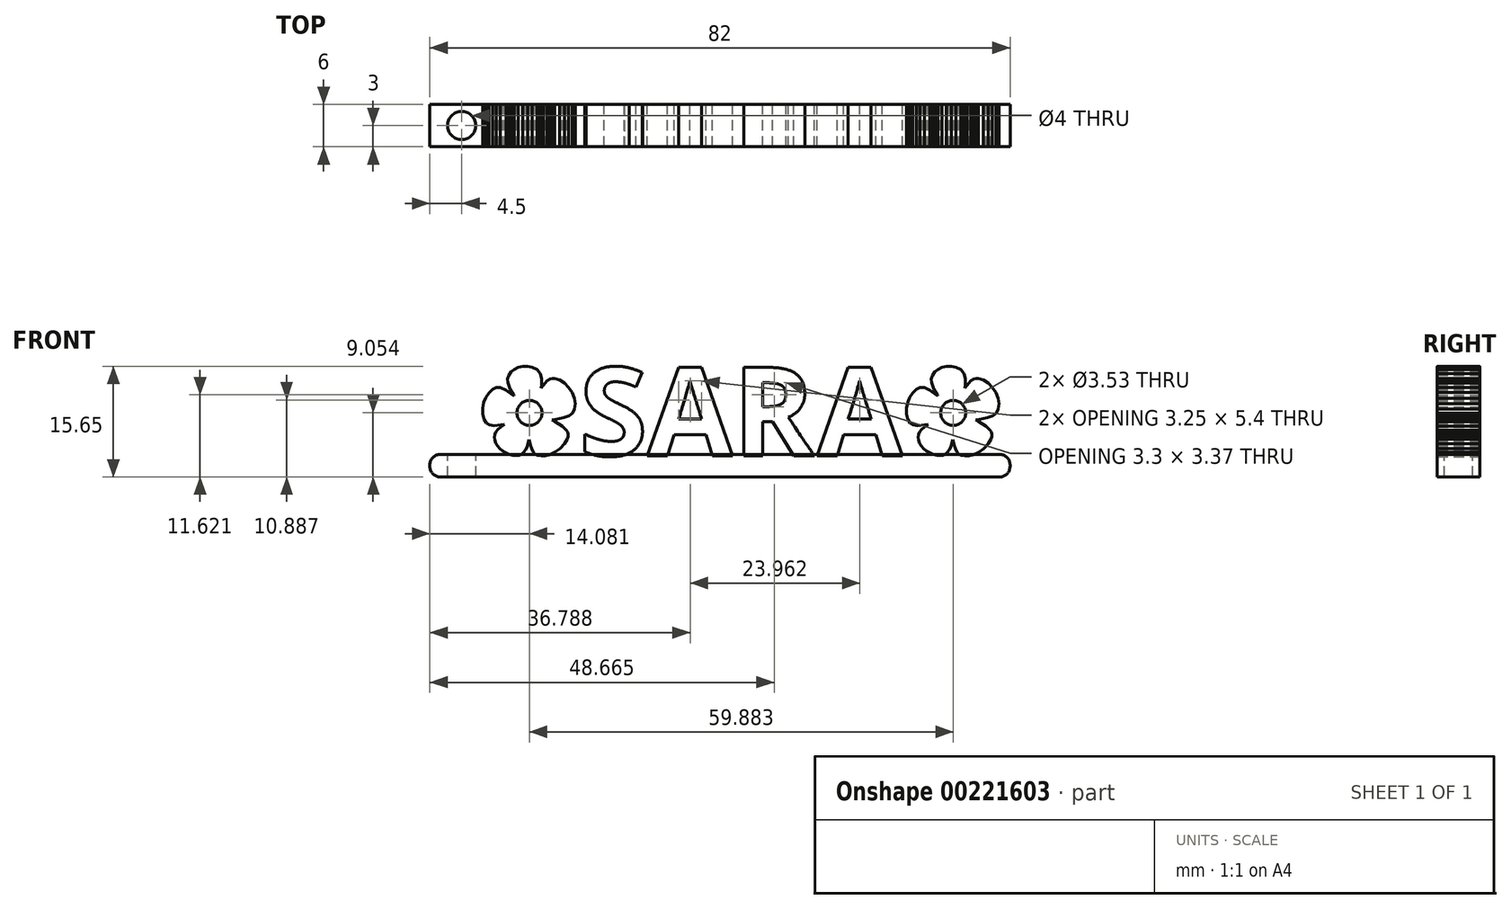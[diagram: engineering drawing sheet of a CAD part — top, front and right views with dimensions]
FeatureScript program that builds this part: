
annotation { "Feature Type Name" : "Feature", "Feature Type Description" : "" }
export const myFeature = defineFeature(function(context is Context, id is Id, definition is map)
    precondition{}
    {
        {
            var Q0;
            Q0=qCreatedBy(makeId("Front.planeOp"),FACE);
            var sketch = newSketch(context, id + "F0", { "sketchPlane" : qUnion([Q0])});
            skText(sketch, "E0", { "text": "   SARA", "fontName": "OpenSans-Bold.ttf"});
            skLineSegment(sketch, "E1.0.0", {"start": v(-9.3, 0.1) * mm, "end": v(-8.53, 0.46) * mm});
            skLineSegment(sketch, "E1.0.1", {"start": v(-8.53, 0.46) * mm, "end": v(-7.79, 1.02) * mm});
            skLineSegment(sketch, "E1.0.2", {"start": v(-7.79, 1.02) * mm, "end": v(-7.18, 1.67) * mm});
            skLineSegment(sketch, "E1.0.3", {"start": v(-7.18, 1.67) * mm, "end": v(-6.78, 2.35) * mm});
            skLineSegment(sketch, "E1.0.4", {"start": v(-6.78, 2.35) * mm, "end": v(-6.68, 2.7) * mm});
            skLineSegment(sketch, "E1.0.5", {"start": v(-6.68, 2.7) * mm, "end": v(-6.67, 3.02) * mm});
            skLineSegment(sketch, "E1.0.6", {"start": v(-6.67, 3.02) * mm, "end": v(-6.73, 3.33) * mm});
            skLineSegment(sketch, "E1.0.7", {"start": v(-6.73, 3.33) * mm, "end": v(-6.89, 3.62) * mm});
            skLineSegment(sketch, "E1.0.8", {"start": v(-6.89, 3.62) * mm, "end": v(-7.48, 4.2) * mm});
            skLineSegment(sketch, "E1.0.9", {"start": v(-7.48, 4.2) * mm, "end": v(-8.5, 4.79) * mm});
            skLineSegment(sketch, "E1.0.10", {"start": v(-8.5, 4.79) * mm, "end": v(-8.93, 5.06) * mm});
            skLineSegment(sketch, "E1.0.11", {"start": v(-8.93, 5.06) * mm, "end": v(-8.42, 5.16) * mm});
            skLineSegment(sketch, "E1.0.12", {"start": v(-8.42, 5.16) * mm, "end": v(-7.31, 5.37) * mm});
            skLineSegment(sketch, "E1.0.13", {"start": v(-7.31, 5.37) * mm, "end": v(-6.55, 5.65) * mm});
            skLineSegment(sketch, "E1.0.14", {"start": v(-6.55, 5.65) * mm, "end": v(-6.05, 6.04) * mm});
            skLineSegment(sketch, "E1.0.15", {"start": v(-6.05, 6.04) * mm, "end": v(-5.76, 6.58) * mm});
            skLineSegment(sketch, "E1.0.16", {"start": v(-5.76, 6.58) * mm, "end": v(-5.64, 7.33) * mm});
            skLineSegment(sketch, "E1.0.17", {"start": v(-5.64, 7.33) * mm, "end": v(-5.78, 8.14) * mm});
            skLineSegment(sketch, "E1.0.18", {"start": v(-5.78, 8.14) * mm, "end": v(-6.1, 8.93) * mm});
            skLineSegment(sketch, "E1.0.19", {"start": v(-6.1, 8.93) * mm, "end": v(-6.6, 9.67) * mm});
            skLineSegment(sketch, "E1.0.20", {"start": v(-6.6, 9.67) * mm, "end": v(-7.2, 10.28) * mm});
            skLineSegment(sketch, "E1.0.21", {"start": v(-7.2, 10.28) * mm, "end": v(-7.86, 10.72) * mm});
            skLineSegment(sketch, "E1.0.22", {"start": v(-7.86, 10.72) * mm, "end": v(-8.55, 10.93) * mm});
            skLineSegment(sketch, "E1.0.23", {"start": v(-8.55, 10.93) * mm, "end": v(-8.88, 10.93) * mm});
            skLineSegment(sketch, "E1.0.24", {"start": v(-8.88, 10.93) * mm, "end": v(-9.2, 10.85) * mm});
            skLineSegment(sketch, "E1.0.25", {"start": v(-9.2, 10.85) * mm, "end": v(-9.65, 10.56) * mm});
            skLineSegment(sketch, "E1.0.26", {"start": v(-9.65, 10.56) * mm, "end": v(-10.14, 9.98) * mm});
            skLineSegment(sketch, "E1.0.27", {"start": v(-10.14, 9.98) * mm, "end": v(-10.45, 9.58) * mm});
            skLineSegment(sketch, "E1.0.28", {"start": v(-10.45, 9.58) * mm, "end": v(-10.4, 10.03) * mm});
            skLineSegment(sketch, "E1.0.29", {"start": v(-10.4, 10.03) * mm, "end": v(-10.4, 10.93) * mm});
            skLineSegment(sketch, "E1.0.30", {"start": v(-10.4, 10.93) * mm, "end": v(-10.6, 11.63) * mm});
            skLineSegment(sketch, "E1.0.31", {"start": v(-10.6, 11.63) * mm, "end": v(-11.04, 12.15) * mm});
            skLineSegment(sketch, "E1.0.32", {"start": v(-11.04, 12.15) * mm, "end": v(-11.71, 12.5) * mm});
            skLineSegment(sketch, "E1.0.33", {"start": v(-11.71, 12.5) * mm, "end": v(-12.4, 12.64) * mm});
            skLineSegment(sketch, "E1.0.34", {"start": v(-12.4, 12.64) * mm, "end": v(-13.07, 12.62) * mm});
            skLineSegment(sketch, "E1.0.35", {"start": v(-13.07, 12.62) * mm, "end": v(-13.7, 12.47) * mm});
            skLineSegment(sketch, "E1.0.36", {"start": v(-13.7, 12.47) * mm, "end": v(-14.26, 12.2) * mm});
            skLineSegment(sketch, "E1.0.37", {"start": v(-14.26, 12.2) * mm, "end": v(-14.72, 11.83) * mm});
            skLineSegment(sketch, "E1.0.38", {"start": v(-14.72, 11.83) * mm, "end": v(-15.05, 11.38) * mm});
            skLineSegment(sketch, "E1.0.39", {"start": v(-15.05, 11.38) * mm, "end": v(-15.22, 10.87) * mm});
            skLineSegment(sketch, "E1.0.40", {"start": v(-15.22, 10.87) * mm, "end": v(-15.2, 10.3) * mm});
            skLineSegment(sketch, "E1.0.41", {"start": v(-15.2, 10.3) * mm, "end": v(-14.83, 9.4) * mm});
            skLineSegment(sketch, "E1.0.42", {"start": v(-14.83, 9.4) * mm, "end": v(-14.35, 8.55) * mm});
            skLineSegment(sketch, "E1.0.43", {"start": v(-14.35, 8.55) * mm, "end": v(-14.3, 8.4) * mm});
            skLineSegment(sketch, "E1.0.44", {"start": v(-14.3, 8.4) * mm, "end": v(-14.48, 8.53) * mm});
            skLineSegment(sketch, "E1.0.45", {"start": v(-14.48, 8.53) * mm, "end": v(-15.4, 9.23) * mm});
            skLineSegment(sketch, "E1.0.46", {"start": v(-15.4, 9.23) * mm, "end": v(-16.22, 9.63) * mm});
            skLineSegment(sketch, "E1.0.47", {"start": v(-16.22, 9.63) * mm, "end": v(-16.8, 9.63) * mm});
            skLineSegment(sketch, "E1.0.48", {"start": v(-16.8, 9.63) * mm, "end": v(-17.36, 9.37) * mm});
            skLineSegment(sketch, "E1.0.49", {"start": v(-17.36, 9.37) * mm, "end": v(-17.85, 8.9) * mm});
            skLineSegment(sketch, "E1.0.50", {"start": v(-17.85, 8.9) * mm, "end": v(-18.26, 8.26) * mm});
            skLineSegment(sketch, "E1.0.51", {"start": v(-18.26, 8.26) * mm, "end": v(-18.56, 7.51) * mm});
            skLineSegment(sketch, "E1.0.52", {"start": v(-18.56, 7.51) * mm, "end": v(-18.72, 6.71) * mm});
            skLineSegment(sketch, "E1.0.53", {"start": v(-18.72, 6.71) * mm, "end": v(-18.72, 5.9) * mm});
            skLineSegment(sketch, "E1.0.54", {"start": v(-18.72, 5.9) * mm, "end": v(-18.52, 5.16) * mm});
            skLineSegment(sketch, "E1.0.55", {"start": v(-18.52, 5.16) * mm, "end": v(-18.2, 4.64) * mm});
            skLineSegment(sketch, "E1.0.56", {"start": v(-18.2, 4.64) * mm, "end": v(-17.75, 4.36) * mm});
            skLineSegment(sketch, "E1.0.57", {"start": v(-17.75, 4.36) * mm, "end": v(-17.1, 4.27) * mm});
            skLineSegment(sketch, "E1.0.58", {"start": v(-17.1, 4.27) * mm, "end": v(-16.21, 4.37) * mm});
            skLineSegment(sketch, "E1.0.59", {"start": v(-16.21, 4.37) * mm, "end": v(-15.7, 4.43) * mm});
            skLineSegment(sketch, "E1.0.60", {"start": v(-15.7, 4.43) * mm, "end": v(-15.67, 4.4) * mm});
            skLineSegment(sketch, "E1.0.61", {"start": v(-15.67, 4.4) * mm, "end": v(-15.78, 4.33) * mm});
            skLineSegment(sketch, "E1.0.62", {"start": v(-15.78, 4.33) * mm, "end": v(-16.17, 4.07) * mm});
            skLineSegment(sketch, "E1.0.63", {"start": v(-16.17, 4.07) * mm, "end": v(-16.55, 3.71) * mm});
            skLineSegment(sketch, "E1.0.64", {"start": v(-16.55, 3.71) * mm, "end": v(-16.87, 3.33) * mm});
            skLineSegment(sketch, "E1.0.65", {"start": v(-16.87, 3.33) * mm, "end": v(-17.04, 3) * mm});
            skLineSegment(sketch, "E1.0.66", {"start": v(-17.04, 3) * mm, "end": v(-17.08, 2.6) * mm});
            skLineSegment(sketch, "E1.0.67", {"start": v(-17.08, 2.6) * mm, "end": v(-17.02, 2.2) * mm});
            skLineSegment(sketch, "E1.0.68", {"start": v(-17.02, 2.2) * mm, "end": v(-16.87, 1.78) * mm});
            skLineSegment(sketch, "E1.0.69", {"start": v(-16.87, 1.78) * mm, "end": v(-16.62, 1.39) * mm});
            skLineSegment(sketch, "E1.0.70", {"start": v(-16.62, 1.39) * mm, "end": v(-16.3, 1.02) * mm});
            skLineSegment(sketch, "E1.0.71", {"start": v(-16.3, 1.02) * mm, "end": v(-15.9, 0.69) * mm});
            skLineSegment(sketch, "E1.0.72", {"start": v(-15.9, 0.69) * mm, "end": v(-15.45, 0.4) * mm});
            skLineSegment(sketch, "E1.0.73", {"start": v(-15.45, 0.4) * mm, "end": v(-14.95, 0.2) * mm});
            skLineSegment(sketch, "E1.0.74", {"start": v(-14.95, 0.2) * mm, "end": v(-14.44, 0.06) * mm});
            skLineSegment(sketch, "E1.0.75", {"start": v(-14.44, 0.06) * mm, "end": v(-13.98, 0.02) * mm});
            skLineSegment(sketch, "E1.0.76", {"start": v(-13.98, 0.02) * mm, "end": v(-13.58, 0.08) * mm});
            skLineSegment(sketch, "E1.0.77", {"start": v(-13.58, 0.08) * mm, "end": v(-13.23, 0.23) * mm});
            skLineSegment(sketch, "E1.0.78", {"start": v(-13.23, 0.23) * mm, "end": v(-12.92, 0.49) * mm});
            skLineSegment(sketch, "E1.0.79", {"start": v(-12.92, 0.49) * mm, "end": v(-12.67, 0.84) * mm});
            skLineSegment(sketch, "E1.0.80", {"start": v(-12.67, 0.84) * mm, "end": v(-12.46, 1.28) * mm});
            skLineSegment(sketch, "E1.0.81", {"start": v(-12.46, 1.28) * mm, "end": v(-12.3, 1.83) * mm});
            skLineSegment(sketch, "E1.0.82", {"start": v(-12.3, 1.83) * mm, "end": v(-12.19, 2.26) * mm});
            skLineSegment(sketch, "E1.0.83", {"start": v(-12.19, 2.26) * mm, "end": v(-12.13, 2.1) * mm});
            skLineSegment(sketch, "E1.0.84", {"start": v(-12.13, 2.1) * mm, "end": v(-12.01, 1.53) * mm});
            skLineSegment(sketch, "E1.0.85", {"start": v(-12.01, 1.53) * mm, "end": v(-11.82, 1) * mm});
            skLineSegment(sketch, "E1.0.86", {"start": v(-11.82, 1) * mm, "end": v(-11.6, 0.55) * mm});
            skLineSegment(sketch, "E1.0.87", {"start": v(-11.6, 0.55) * mm, "end": v(-11.35, 0.26) * mm});
            skLineSegment(sketch, "E1.0.88", {"start": v(-11.35, 0.26) * mm, "end": v(-10.95, 0.05) * mm});
            skLineSegment(sketch, "E1.0.89", {"start": v(-10.95, 0.05) * mm, "end": v(-10.46, -0.04) * mm});
            skLineSegment(sketch, "E1.0.90", {"start": v(-10.46, -0.04) * mm, "end": v(-9.9, -0.03) * mm});
            skLineSegment(sketch, "E1.0.91", {"start": v(-9.9, -0.03) * mm, "end": v(-9.3, 0.1) * mm});
            skCircle(sketch, "E2", {"center": v(-12.12, 6.05) * mm, "radius": 1.77 * mm});
            skCircle(sketch, "E3.1.0.0", {"center": v(47.76, 6.05) * mm, "radius": 1.77 * mm});
            skLineSegment(sketch, "E3.1.0.1", {"start": v(49.43, 9.58) * mm, "end": v(49.48, 10.03) * mm});
            skLineSegment(sketch, "E3.1.0.2", {"start": v(52.69, 10.28) * mm, "end": v(52.02, 10.72) * mm});
            skLineSegment(sketch, "E3.1.0.3", {"start": v(41.17, 5.9) * mm, "end": v(41.37, 5.16) * mm});
            skLineSegment(sketch, "E3.1.0.4", {"start": v(45.62, 12.2) * mm, "end": v(45.16, 11.83) * mm});
            skLineSegment(sketch, "E3.1.0.5", {"start": v(43.58, 1.02) * mm, "end": v(43.98, 0.69) * mm});
            skLineSegment(sketch, "E3.1.0.6", {"start": v(43.67, 9.63) * mm, "end": v(43.08, 9.63) * mm});
            skLineSegment(sketch, "E3.1.0.7", {"start": v(41.32, 7.51) * mm, "end": v(41.16, 6.71) * mm});
            skLineSegment(sketch, "E3.1.0.8", {"start": v(44.49, 9.23) * mm, "end": v(43.67, 9.63) * mm});
            skLineSegment(sketch, "E3.1.0.9", {"start": v(43.08, 9.63) * mm, "end": v(42.53, 9.37) * mm});
            skLineSegment(sketch, "E3.1.0.10", {"start": v(49.74, 9.98) * mm, "end": v(49.43, 9.58) * mm});
            skLineSegment(sketch, "E3.1.0.11", {"start": v(49.28, 11.63) * mm, "end": v(48.85, 12.15) * mm});
            skLineSegment(sketch, "E3.1.0.12", {"start": v(48.85, 12.15) * mm, "end": v(48.17, 12.5) * mm});
            skLineSegment(sketch, "E3.1.0.13", {"start": v(49.5, 10.93) * mm, "end": v(49.28, 11.63) * mm});
            skLineSegment(sketch, "E3.1.0.14", {"start": v(44.43, 0.4) * mm, "end": v(44.94, 0.2) * mm});
            skLineSegment(sketch, "E3.1.0.15", {"start": v(49.99, -0.03) * mm, "end": v(50.57, 0.1) * mm});
            skLineSegment(sketch, "E3.1.0.16", {"start": v(41.16, 6.71) * mm, "end": v(41.17, 5.9) * mm});
            skLineSegment(sketch, "E3.1.0.17", {"start": v(50.57, 0.1) * mm, "end": v(51.35, 0.46) * mm});
            skLineSegment(sketch, "E3.1.0.18", {"start": v(43.98, 0.69) * mm, "end": v(44.43, 0.4) * mm});
            skLineSegment(sketch, "E3.1.0.19", {"start": v(41.37, 5.16) * mm, "end": v(41.68, 4.64) * mm});
            skLineSegment(sketch, "E3.1.0.20", {"start": v(52.57, 5.37) * mm, "end": v(53.34, 5.65) * mm});
            skLineSegment(sketch, "E3.1.0.21", {"start": v(51.35, 0.46) * mm, "end": v(52.1, 1.02) * mm});
            skLineSegment(sketch, "E3.1.0.22", {"start": v(53.29, 9.67) * mm, "end": v(52.69, 10.28) * mm});
            skLineSegment(sketch, "E3.1.0.23", {"start": v(49.48, 10.03) * mm, "end": v(49.5, 10.93) * mm});
            skLineSegment(sketch, "E3.1.0.24", {"start": v(42.53, 9.37) * mm, "end": v(42.03, 8.9) * mm});
            skLineSegment(sketch, "E3.1.0.25", {"start": v(48.17, 12.5) * mm, "end": v(47.49, 12.64) * mm});
            skLineSegment(sketch, "E3.1.0.26", {"start": v(46.81, 12.62) * mm, "end": v(46.18, 12.47) * mm});
            skLineSegment(sketch, "E3.1.0.27", {"start": v(52.7, 1.67) * mm, "end": v(53.1, 2.35) * mm});
            skLineSegment(sketch, "E3.1.0.28", {"start": v(53.77, 8.93) * mm, "end": v(53.29, 9.67) * mm});
            skLineSegment(sketch, "E3.1.0.29", {"start": v(47.49, 12.64) * mm, "end": v(46.81, 12.62) * mm});
            skLineSegment(sketch, "E3.1.0.30", {"start": v(52.1, 1.02) * mm, "end": v(52.7, 1.67) * mm});
            skLineSegment(sketch, "E3.1.0.31", {"start": v(42.03, 8.9) * mm, "end": v(41.62, 8.26) * mm});
            skLineSegment(sketch, "E3.1.0.32", {"start": v(41.62, 8.26) * mm, "end": v(41.32, 7.51) * mm});
            skLineSegment(sketch, "E3.1.0.33", {"start": v(46.18, 12.47) * mm, "end": v(45.62, 12.2) * mm});
            skLineSegment(sketch, "E3.1.0.34", {"start": v(53.1, 2.35) * mm, "end": v(53.2, 2.7) * mm});
            skLineSegment(sketch, "E3.1.0.35", {"start": v(43.08, 9.63) * mm, "end": v(42.53, 9.37) * mm});
            skLineSegment(sketch, "E3.1.0.36", {"start": v(47.49, 12.64) * mm, "end": v(46.81, 12.62) * mm});
            skLineSegment(sketch, "E3.1.0.37", {"start": v(52.57, 5.37) * mm, "end": v(53.34, 5.65) * mm});
            skLineSegment(sketch, "E3.1.0.38", {"start": v(48.93, 0.05) * mm, "end": v(49.43, -0.04) * mm});
            skLineSegment(sketch, "E3.1.0.39", {"start": v(53.77, 8.93) * mm, "end": v(53.29, 9.67) * mm});
            skLineSegment(sketch, "E3.1.0.40", {"start": v(49.99, -0.03) * mm, "end": v(50.57, 0.1) * mm});
            skLineSegment(sketch, "E3.1.0.41", {"start": v(49.74, 9.98) * mm, "end": v(49.43, 9.58) * mm});
            skLineSegment(sketch, "E3.1.0.42", {"start": v(52.1, 1.02) * mm, "end": v(52.7, 1.67) * mm});
            skLineSegment(sketch, "E3.1.0.43", {"start": v(53.1, 2.35) * mm, "end": v(53.2, 2.7) * mm});
            skLineSegment(sketch, "E3.1.0.44", {"start": v(41.16, 6.71) * mm, "end": v(41.17, 5.9) * mm});
            skLineSegment(sketch, "E3.1.0.45", {"start": v(50.57, 0.1) * mm, "end": v(51.35, 0.46) * mm});
            skLineSegment(sketch, "E3.1.0.46", {"start": v(46.81, 12.62) * mm, "end": v(46.18, 12.47) * mm});
            skLineSegment(sketch, "E3.1.0.47", {"start": v(45.62, 12.2) * mm, "end": v(45.16, 11.83) * mm});
            skLineSegment(sketch, "E3.1.0.48", {"start": v(44.43, 0.4) * mm, "end": v(44.94, 0.2) * mm});
            skLineSegment(sketch, "E3.1.0.49", {"start": v(49.48, 10.03) * mm, "end": v(49.5, 10.93) * mm});
            skLineSegment(sketch, "E3.1.0.50", {"start": v(49.43, 9.58) * mm, "end": v(49.48, 10.03) * mm});
            skLineSegment(sketch, "E3.1.0.51", {"start": v(49.43, -0.04) * mm, "end": v(49.99, -0.03) * mm});
            skLineSegment(sketch, "E3.1.0.52", {"start": v(43.67, 9.63) * mm, "end": v(43.08, 9.63) * mm});
            skLineSegment(sketch, "E3.1.0.53", {"start": v(49.5, 10.93) * mm, "end": v(49.28, 11.63) * mm});
            skLineSegment(sketch, "E3.1.0.54", {"start": v(52.69, 10.28) * mm, "end": v(52.02, 10.72) * mm});
            skLineSegment(sketch, "E3.1.0.55", {"start": v(42.03, 8.9) * mm, "end": v(41.62, 8.26) * mm});
            skLineSegment(sketch, "E3.1.0.56", {"start": v(43.98, 0.69) * mm, "end": v(44.43, 0.4) * mm});
            skLineSegment(sketch, "E3.1.0.57", {"start": v(48.17, 12.5) * mm, "end": v(47.49, 12.64) * mm});
            skLineSegment(sketch, "E3.1.0.58", {"start": v(42.53, 9.37) * mm, "end": v(42.03, 8.9) * mm});
            skLineSegment(sketch, "E3.1.0.59", {"start": v(41.17, 5.9) * mm, "end": v(41.37, 5.16) * mm});
            skLineSegment(sketch, "E3.1.0.60", {"start": v(48.85, 12.15) * mm, "end": v(48.17, 12.5) * mm});
            skLineSegment(sketch, "E3.1.0.61", {"start": v(44.49, 9.23) * mm, "end": v(43.67, 9.63) * mm});
            skLineSegment(sketch, "E3.1.0.62", {"start": v(51.35, 0.46) * mm, "end": v(52.1, 1.02) * mm});
            skLineSegment(sketch, "E3.1.0.63", {"start": v(49.28, 11.63) * mm, "end": v(48.85, 12.15) * mm});
            skLineSegment(sketch, "E3.1.0.64", {"start": v(41.62, 8.26) * mm, "end": v(41.32, 7.51) * mm});
            skLineSegment(sketch, "E3.1.0.65", {"start": v(52.7, 1.67) * mm, "end": v(53.1, 2.35) * mm});
            skLineSegment(sketch, "E3.1.0.66", {"start": v(41.32, 7.51) * mm, "end": v(41.16, 6.71) * mm});
            skLineSegment(sketch, "E3.1.0.67", {"start": v(43.58, 1.02) * mm, "end": v(43.98, 0.69) * mm});
            skLineSegment(sketch, "E3.1.0.68", {"start": v(41.37, 5.16) * mm, "end": v(41.68, 4.64) * mm});
            skLineSegment(sketch, "E3.1.0.69", {"start": v(46.18, 12.47) * mm, "end": v(45.62, 12.2) * mm});
            skLineSegment(sketch, "E3.1.0.70", {"start": v(53.29, 9.67) * mm, "end": v(52.69, 10.28) * mm});
            skLineSegment(sketch, "E3.1.0.71", {"start": v(45.16, 11.83) * mm, "end": v(44.83, 11.38) * mm});
            skLineSegment(sketch, "E3.1.0.72", {"start": v(52.02, 10.72) * mm, "end": v(51.34, 10.93) * mm});
            skLineSegment(sketch, "E3.1.0.73", {"start": v(53.83, 6.04) * mm, "end": v(54.13, 6.58) * mm});
            skLineSegment(sketch, "E3.1.0.74", {"start": v(53.2, 2.7) * mm, "end": v(53.22, 3.02) * mm});
            skLineSegment(sketch, "E3.1.0.75", {"start": v(51.34, 10.93) * mm, "end": v(51, 10.93) * mm});
            skLineSegment(sketch, "E3.1.0.76", {"start": v(41.68, 4.64) * mm, "end": v(42.13, 4.36) * mm});
            skLineSegment(sketch, "E3.1.0.77", {"start": v(50.68, 10.85) * mm, "end": v(50.24, 10.56) * mm});
            skLineSegment(sketch, "E3.1.0.78", {"start": v(51.47, 5.16) * mm, "end": v(52.57, 5.37) * mm});
            skLineSegment(sketch, "E3.1.0.79", {"start": v(53.22, 3.02) * mm, "end": v(53.15, 3.33) * mm});
            skLineSegment(sketch, "E3.1.0.80", {"start": v(53.15, 3.33) * mm, "end": v(53, 3.62) * mm});
            skLineSegment(sketch, "E3.1.0.81", {"start": v(52.4, 4.2) * mm, "end": v(51.39, 4.79) * mm});
            skLineSegment(sketch, "E3.1.0.82", {"start": v(54.24, 7.33) * mm, "end": v(54.1, 8.14) * mm});
            skLineSegment(sketch, "E3.1.0.83", {"start": v(43.26, 1.39) * mm, "end": v(43.58, 1.02) * mm});
            skLineSegment(sketch, "E3.1.0.84", {"start": v(45.44, 0.06) * mm, "end": v(45.9, 0.02) * mm});
            skLineSegment(sketch, "E3.1.0.85", {"start": v(50.96, 5.06) * mm, "end": v(51.47, 5.16) * mm});
            skLineSegment(sketch, "E3.1.0.86", {"start": v(48.53, 0.26) * mm, "end": v(48.93, 0.05) * mm});
            skLineSegment(sketch, "E3.1.0.87", {"start": v(44.83, 11.38) * mm, "end": v(44.66, 10.87) * mm});
            skLineSegment(sketch, "E3.1.0.88", {"start": v(54.13, 6.58) * mm, "end": v(54.24, 7.33) * mm});
            skLineSegment(sketch, "E3.1.0.89", {"start": v(48.93, 0.05) * mm, "end": v(49.43, -0.04) * mm});
            skLineSegment(sketch, "E3.1.0.90", {"start": v(51.39, 4.79) * mm, "end": v(50.96, 5.06) * mm});
            skLineSegment(sketch, "E3.1.0.91", {"start": v(44.94, 0.2) * mm, "end": v(45.44, 0.06) * mm});
            skLineSegment(sketch, "E3.1.0.92", {"start": v(44.69, 10.3) * mm, "end": v(45.05, 9.4) * mm});
            skLineSegment(sketch, "E3.1.0.93", {"start": v(43.02, 1.78) * mm, "end": v(43.26, 1.39) * mm});
            skLineSegment(sketch, "E3.1.0.94", {"start": v(53, 3.62) * mm, "end": v(52.4, 4.2) * mm});
            skLineSegment(sketch, "E3.1.0.95", {"start": v(49.43, -0.04) * mm, "end": v(49.99, -0.03) * mm});
            skLineSegment(sketch, "E3.1.0.96", {"start": v(44.66, 10.87) * mm, "end": v(44.69, 10.3) * mm});
            skLineSegment(sketch, "E3.1.0.97", {"start": v(53.34, 5.65) * mm, "end": v(53.83, 6.04) * mm});
            skLineSegment(sketch, "E3.1.0.98", {"start": v(51, 10.93) * mm, "end": v(50.68, 10.85) * mm});
            skLineSegment(sketch, "E3.1.0.99", {"start": v(50.24, 10.56) * mm, "end": v(49.74, 9.98) * mm});
            skLineSegment(sketch, "E3.1.0.100", {"start": v(45.9, 0.02) * mm, "end": v(46.3, 0.08) * mm});
            skLineSegment(sketch, "E3.1.0.101", {"start": v(42.86, 2.2) * mm, "end": v(43.02, 1.78) * mm});
            skLineSegment(sketch, "E3.1.0.102", {"start": v(54.1, 8.14) * mm, "end": v(53.77, 8.93) * mm});
            skLineSegment(sketch, "E3.1.0.103", {"start": v(51.39, 4.79) * mm, "end": v(50.96, 5.06) * mm});
            skLineSegment(sketch, "E3.1.0.104", {"start": v(50.96, 5.06) * mm, "end": v(51.47, 5.16) * mm});
            skLineSegment(sketch, "E3.1.0.105", {"start": v(41.68, 4.64) * mm, "end": v(42.13, 4.36) * mm});
            skLineSegment(sketch, "E3.1.0.106", {"start": v(48.29, 0.55) * mm, "end": v(48.53, 0.26) * mm});
            skLineSegment(sketch, "E3.1.0.107", {"start": v(48.53, 0.26) * mm, "end": v(48.93, 0.05) * mm});
            skLineSegment(sketch, "E3.1.0.108", {"start": v(43.02, 1.78) * mm, "end": v(43.26, 1.39) * mm});
            skLineSegment(sketch, "E3.1.0.109", {"start": v(53, 3.62) * mm, "end": v(52.4, 4.2) * mm});
            skLineSegment(sketch, "E3.1.0.110", {"start": v(51.47, 5.16) * mm, "end": v(52.57, 5.37) * mm});
            skLineSegment(sketch, "E3.1.0.111", {"start": v(44.69, 10.3) * mm, "end": v(45.05, 9.4) * mm});
            skLineSegment(sketch, "E3.1.0.112", {"start": v(53.34, 5.65) * mm, "end": v(53.83, 6.04) * mm});
            skLineSegment(sketch, "E3.1.0.113", {"start": v(50.24, 10.56) * mm, "end": v(49.74, 9.98) * mm});
            skLineSegment(sketch, "E3.1.0.114", {"start": v(54.13, 6.58) * mm, "end": v(54.24, 7.33) * mm});
            skLineSegment(sketch, "E3.1.0.115", {"start": v(44.66, 10.87) * mm, "end": v(44.69, 10.3) * mm});
            skLineSegment(sketch, "E3.1.0.116", {"start": v(51, 10.93) * mm, "end": v(50.68, 10.85) * mm});
            skLineSegment(sketch, "E3.1.0.117", {"start": v(45.9, 0.02) * mm, "end": v(46.3, 0.08) * mm});
            skLineSegment(sketch, "E3.1.0.118", {"start": v(50.68, 10.85) * mm, "end": v(50.24, 10.56) * mm});
            skLineSegment(sketch, "E3.1.0.119", {"start": v(45.44, 0.06) * mm, "end": v(45.9, 0.02) * mm});
            skLineSegment(sketch, "E3.1.0.120", {"start": v(44.94, 0.2) * mm, "end": v(45.44, 0.06) * mm});
            skLineSegment(sketch, "E3.1.0.121", {"start": v(52.4, 4.2) * mm, "end": v(51.39, 4.79) * mm});
            skLineSegment(sketch, "E3.1.0.122", {"start": v(53.83, 6.04) * mm, "end": v(54.13, 6.58) * mm});
            skLineSegment(sketch, "E3.1.0.123", {"start": v(42.8, 2.6) * mm, "end": v(42.86, 2.2) * mm});
            skLineSegment(sketch, "E3.1.0.124", {"start": v(53.2, 2.7) * mm, "end": v(53.22, 3.02) * mm});
            skLineSegment(sketch, "E3.1.0.125", {"start": v(43.26, 1.39) * mm, "end": v(43.58, 1.02) * mm});
            skLineSegment(sketch, "E3.1.0.126", {"start": v(54.1, 8.14) * mm, "end": v(53.77, 8.93) * mm});
            skLineSegment(sketch, "E3.1.0.127", {"start": v(54.24, 7.33) * mm, "end": v(54.1, 8.14) * mm});
            skLineSegment(sketch, "E3.1.0.128", {"start": v(53.22, 3.02) * mm, "end": v(53.15, 3.33) * mm});
            skLineSegment(sketch, "E3.1.0.129", {"start": v(42.86, 2.2) * mm, "end": v(43.02, 1.78) * mm});
            skLineSegment(sketch, "E3.1.0.130", {"start": v(53.15, 3.33) * mm, "end": v(53, 3.62) * mm});
            skLineSegment(sketch, "E3.1.0.131", {"start": v(44.83, 11.38) * mm, "end": v(44.66, 10.87) * mm});
            skLineSegment(sketch, "E3.1.0.132", {"start": v(51.34, 10.93) * mm, "end": v(51, 10.93) * mm});
            skLineSegment(sketch, "E3.1.0.133", {"start": v(52.02, 10.72) * mm, "end": v(51.34, 10.93) * mm});
            skLineSegment(sketch, "E3.1.0.134", {"start": v(45.16, 11.83) * mm, "end": v(44.83, 11.38) * mm});
            skLineSegment(sketch, "E3.1.0.135", {"start": v(42.8, 2.6) * mm, "end": v(42.86, 2.2) * mm});
            skLineSegment(sketch, "E3.1.0.136", {"start": v(43.67, 4.37) * mm, "end": v(44.18, 4.43) * mm});
            skLineSegment(sketch, "E3.1.0.137", {"start": v(47.87, 1.53) * mm, "end": v(48.06, 1) * mm});
            skLineSegment(sketch, "E3.1.0.138", {"start": v(44.1, 4.33) * mm, "end": v(43.72, 4.07) * mm});
            skLineSegment(sketch, "E3.1.0.139", {"start": v(46.66, 0.23) * mm, "end": v(46.96, 0.49) * mm});
            skLineSegment(sketch, "E3.1.0.140", {"start": v(47.22, 0.84) * mm, "end": v(47.42, 1.28) * mm});
            skLineSegment(sketch, "E3.1.0.141", {"start": v(48.06, 1) * mm, "end": v(48.29, 0.55) * mm});
            skLineSegment(sketch, "E3.1.0.142", {"start": v(43.72, 4.07) * mm, "end": v(43.33, 3.71) * mm});
            skLineSegment(sketch, "E3.1.0.143", {"start": v(47.75, 2.1) * mm, "end": v(47.87, 1.53) * mm});
            skLineSegment(sketch, "E3.1.0.144", {"start": v(46.96, 0.49) * mm, "end": v(47.22, 0.84) * mm});
            skLineSegment(sketch, "E3.1.0.145", {"start": v(42.77, 4.27) * mm, "end": v(43.67, 4.37) * mm});
            skLineSegment(sketch, "E3.1.0.146", {"start": v(43.33, 3.71) * mm, "end": v(43.02, 3.33) * mm});
            skLineSegment(sketch, "E3.1.0.147", {"start": v(42.13, 4.36) * mm, "end": v(42.77, 4.27) * mm});
            skLineSegment(sketch, "E3.1.0.148", {"start": v(47.42, 1.28) * mm, "end": v(47.58, 1.83) * mm});
            skLineSegment(sketch, "E3.1.0.149", {"start": v(47.7, 2.26) * mm, "end": v(47.75, 2.1) * mm});
            skLineSegment(sketch, "E3.1.0.150", {"start": v(43.02, 3.33) * mm, "end": v(42.85, 3) * mm});
            skLineSegment(sketch, "E3.1.0.151", {"start": v(48.29, 0.55) * mm, "end": v(48.53, 0.26) * mm});
            skLineSegment(sketch, "E3.1.0.152", {"start": v(47.58, 1.83) * mm, "end": v(47.7, 2.26) * mm});
            skLineSegment(sketch, "E3.1.0.153", {"start": v(42.85, 3) * mm, "end": v(42.8, 2.6) * mm});
            skLineSegment(sketch, "E3.1.0.154", {"start": v(46.3, 0.08) * mm, "end": v(46.66, 0.23) * mm});
            skLineSegment(sketch, "E3.1.0.155", {"start": v(44.21, 4.4) * mm, "end": v(44.1, 4.33) * mm});
            skLineSegment(sketch, "E3.1.0.156", {"start": v(47.7, 2.26) * mm, "end": v(47.75, 2.1) * mm});
            skLineSegment(sketch, "E3.1.0.157", {"start": v(42.77, 4.27) * mm, "end": v(43.67, 4.37) * mm});
            skLineSegment(sketch, "E3.1.0.158", {"start": v(47.87, 1.53) * mm, "end": v(48.06, 1) * mm});
            skLineSegment(sketch, "E3.1.0.159", {"start": v(44.18, 4.43) * mm, "end": v(44.21, 4.4) * mm});
            skLineSegment(sketch, "E3.1.0.160", {"start": v(43.33, 3.71) * mm, "end": v(43.02, 3.33) * mm});
            skLineSegment(sketch, "E3.1.0.161", {"start": v(42.13, 4.36) * mm, "end": v(42.77, 4.27) * mm});
            skLineSegment(sketch, "E3.1.0.162", {"start": v(43.67, 4.37) * mm, "end": v(44.18, 4.43) * mm});
            skLineSegment(sketch, "E3.1.0.163", {"start": v(46.3, 0.08) * mm, "end": v(46.66, 0.23) * mm});
            skLineSegment(sketch, "E3.1.0.164", {"start": v(43.72, 4.07) * mm, "end": v(43.33, 3.71) * mm});
            skLineSegment(sketch, "E3.1.0.165", {"start": v(47.75, 2.1) * mm, "end": v(47.87, 1.53) * mm});
            skLineSegment(sketch, "E3.1.0.166", {"start": v(47.58, 1.83) * mm, "end": v(47.7, 2.26) * mm});
            skLineSegment(sketch, "E3.1.0.167", {"start": v(44.1, 4.33) * mm, "end": v(43.72, 4.07) * mm});
            skLineSegment(sketch, "E3.1.0.168", {"start": v(46.66, 0.23) * mm, "end": v(46.96, 0.49) * mm});
            skLineSegment(sketch, "E3.1.0.169", {"start": v(42.85, 3) * mm, "end": v(42.8, 2.6) * mm});
            skLineSegment(sketch, "E3.1.0.170", {"start": v(48.06, 1) * mm, "end": v(48.29, 0.55) * mm});
            skLineSegment(sketch, "E3.1.0.171", {"start": v(46.96, 0.49) * mm, "end": v(47.22, 0.84) * mm});
            skLineSegment(sketch, "E3.1.0.172", {"start": v(47.22, 0.84) * mm, "end": v(47.42, 1.28) * mm});
            skLineSegment(sketch, "E3.1.0.173", {"start": v(43.02, 3.33) * mm, "end": v(42.85, 3) * mm});
            skLineSegment(sketch, "E3.1.0.174", {"start": v(47.42, 1.28) * mm, "end": v(47.58, 1.83) * mm});
            skLineSegment(sketch, "E3.1.0.175", {"start": v(44.21, 4.4) * mm, "end": v(44.1, 4.33) * mm});
            skLineSegment(sketch, "E3.1.0.176", {"start": v(44.18, 4.43) * mm, "end": v(44.21, 4.4) * mm});
            skLineSegment(sketch, "E3.1.0.177", {"start": v(45.6, 8.4) * mm, "end": v(45.4, 8.53) * mm});
            skLineSegment(sketch, "E3.1.0.178", {"start": v(45.53, 8.55) * mm, "end": v(45.6, 8.4) * mm});
            skLineSegment(sketch, "E3.1.0.179", {"start": v(45.05, 9.4) * mm, "end": v(45.53, 8.55) * mm});
            skLineSegment(sketch, "E3.1.0.180", {"start": v(45.4, 8.53) * mm, "end": v(44.49, 9.23) * mm});
            skLineSegment(sketch, "E3.1.0.181", {"start": v(45.53, 8.55) * mm, "end": v(45.6, 8.4) * mm});
            skLineSegment(sketch, "E3.1.0.182", {"start": v(45.05, 9.4) * mm, "end": v(45.53, 8.55) * mm});
            skLineSegment(sketch, "E3.1.0.183", {"start": v(45.4, 8.53) * mm, "end": v(44.49, 9.23) * mm});
            skLineSegment(sketch, "E3.1.0.184", {"start": v(45.6, 8.4) * mm, "end": v(45.4, 8.53) * mm});
            skLineSegment(sketch, "E3.direction1", {"start": v(-16.3, 1.02) * mm, "end": v(42.4, 1.02) * mm, "construction": true});
            const initialGuessF0  = {"E0": [-0.0187, 0, 1, 0, 0.01258]};
            skSetInitialGuess(sketch, initialGuessF0);
            skSolve(sketch);
        }
        {
            var Q0;
            Q0=qSketchRegion(id+"F0",true);
            extrude(context, id + "F1", {"entities" : qUnion([Q0]), "endBound" : BoundingType.SYMMETRIC, "depth" : 6 * mm});
        }
        {
            var Q0;
            Q0=qCreatedBy(makeId("Top.planeOp"),FACE);
            var sketch = newSketch(context, id + "F2", { "sketchPlane" : qUnion([Q0])});
            skLineSegment(sketch, "E4.bottom", {"start": v(-18.7, 3) * mm, "end": v(55.8, 3) * mm});
            skLineSegment(sketch, "E4.top", {"start": v(-18.7, -3) * mm, "end": v(55.8, -3) * mm});
            skLineSegment(sketch, "E4.left", {"start": v(-18.7, 3) * mm, "end": v(-18.7, -3) * mm});
            skLineSegment(sketch, "E4.right", {"start": v(55.8, 3) * mm, "end": v(55.8, -3) * mm});
            skSolve(sketch);
        }
        {
            var Q0;
            Q0=makeQuery(id+"F2.imprint","IMPRINT",FACE,{"disambiguationData":[TD([[makeQuery(id+"F2.imprint","IMPRINT",EDGE,{"derivedFrom":sQuery(id+"F2.wireOp",EDGE,"E4.bottom")}),-1.0]])]});
            extrude(context, id + "F3", {"entities" : qUnion([Q0]), "depth" : 0.2 * mm});
        }
        {
            var Q0;
            Q0=makeQuery(id+"F3.opExtrude","CAP_FACE",FACE,{"disambiguationData":[OSD([sQuery(id+"F2.wireOp",EDGE,"E4.bottom"),sQuery(id+"F2.wireOp",EDGE,"E4.top"),sQuery(id+"F2.wireOp",EDGE,"E4.left"),sQuery(id+"F2.wireOp",EDGE,"E4.right")])],"isStart":true});
            extrude(context, id + "F4", {"entities" : qUnion([Q0]), "depth" : 3 * mm});
        }
        {
            var Q0;
            {var subQ0=sQuery(id+"F2.wireOp",EDGE,"E4.left");Q0=makeQuery(id+"FaVoHrOpcFZXiYX_6.opBoolean","MERGE",FACE,{"derivedFrom":[makeQuery(id+"F3.opExtrude","SWEPT_FACE",FACE,{"disambiguationData":[OSD([subQ0])]}),makeQuery(id+"F4.opExtrude","SWEPT_FACE",FACE,{"disambiguationData":[OSD([subQ0])]})]});}
            var sketch = newSketch(context, id + "F5", { "sketchPlane" : qUnion([Q0])});
            skLineSegment(sketch, "E5.bottom", {"start": v(-3, -3) * mm, "end": v(3, -3) * mm});
            skLineSegment(sketch, "E5.top", {"start": v(-3, 0.2) * mm, "end": v(3, 0.2) * mm});
            skLineSegment(sketch, "E5.left", {"start": v(-3, -3) * mm, "end": v(-3, 0.2) * mm});
            skLineSegment(sketch, "E5.right", {"start": v(3, -3) * mm, "end": v(3, 0.2) * mm});
            skSolve(sketch);
        }
        {
            var Q0;
            Q0=qSketchRegion(id+"F5",true);
            extrude(context, id + "F6", {"entities" : qUnion([Q0]), "operationType" : NewBodyOperationType.ADD, "depth" : 7.5 * mm});
        }
        {
            var Q0;
            Q0=makeQuery(id+"F6.opExtrude","CAP_EDGE",EDGE,{"disambiguationData":[OSD([sQuery(id+"F5.wireOp",EDGE,"E5.bottom")])],"isStart":false});
            var Q1;
            Q1=makeQuery(id+"F6.opExtrude","CAP_EDGE",EDGE,{"disambiguationData":[OSD([sQuery(id+"F5.wireOp",EDGE,"E5.top")])],"isStart":false});
            var Q2;
            Q2=makeQuery(id+"F4.opExtrude","CAP_EDGE",EDGE,{"disambiguationData":[OSD([sQuery(id+"F2.wireOp",EDGE,"E4.right")])],"isStart":false});
            fillet(context, id + "F7", {"entities" : qUnion([Q0, Q1, Q2]), "radius" : 1.5 * mm, "tangentPropagation" : true, "allowEdgeOverflow" : false});
        }
        {
            var Q0;
            {var subQ19=sQuery(id+"F2.wireOp",EDGE,"E4.top");var subQ20=sQuery(id+"F2.wireOp",EDGE,"E4.bottom");var subQ63=sQuery(id+"F0.wireOp",EDGE,"E0.sketch_text.stroke-2");var subQ66=sQuery(id+"F2.wireOp",EDGE,"E4.left");Q0=makeQuery(id+"F6.boolean.opBoolean","MERGE",FACE,{"derivedFrom":[makeQuery(id+"FaVoHrOpcFZXiYX_6.opBoolean","SPLIT",FACE,{"disambiguationData":[TD([makeQuery(id+"F1.opExtrude","SWEPT_FACE",FACE,{"disambiguationData":[OSD([subQ63])]})])],"derivedFrom":makeQuery(id+"F3.opExtrude","CAP_FACE",FACE,{"disambiguationData":[OSD([subQ20,subQ19,subQ66,sQuery(id+"F2.wireOp",EDGE,"E4.right")])],"isStart":false})}),makeQuery(id+"F6.opExtrude","SWEPT_FACE",FACE,{"disambiguationData":[OSD([sQuery(id+"F5.wireOp",EDGE,"E5.top")])]})]});}
            var sketch = newSketch(context, id + "F8", { "sketchPlane" : qUnion([Q0])});
            skCircle(sketch, "E6", {"center": v(-21.7, 0) * mm, "radius": 2 * mm});
            skSolve(sketch);
        }
        {
            var Q0;
            Q0=makeQuery(id+"F8.imprint","IMPRINT",FACE,{"disambiguationData":[TD([[makeQuery(id+"F8.imprint","IMPRINT",EDGE,{"derivedFrom":sQuery(id+"F8.wireOp",EDGE,"E6")}),1.0]])]});
            extrude(context, id + "F9", {"entities" : qUnion([Q0]), "operationType" : NewBodyOperationType.REMOVE, "oppositeDirection" : true, "depth" : 4 * mm});
        }
        {
            var Q0;
            Q0=makeQuery(id+"F3.opExtrude","CAP_EDGE",EDGE,{"disambiguationData":[OSD([sQuery(id+"F2.wireOp",EDGE,"E4.right")])],"isStart":false});
            fillet(context, id + "F10", {"entities" : qUnion([Q0]), "radius" : 1.5 * mm, "tangentPropagation" : true, "allowEdgeOverflow" : false});
        }
    });
